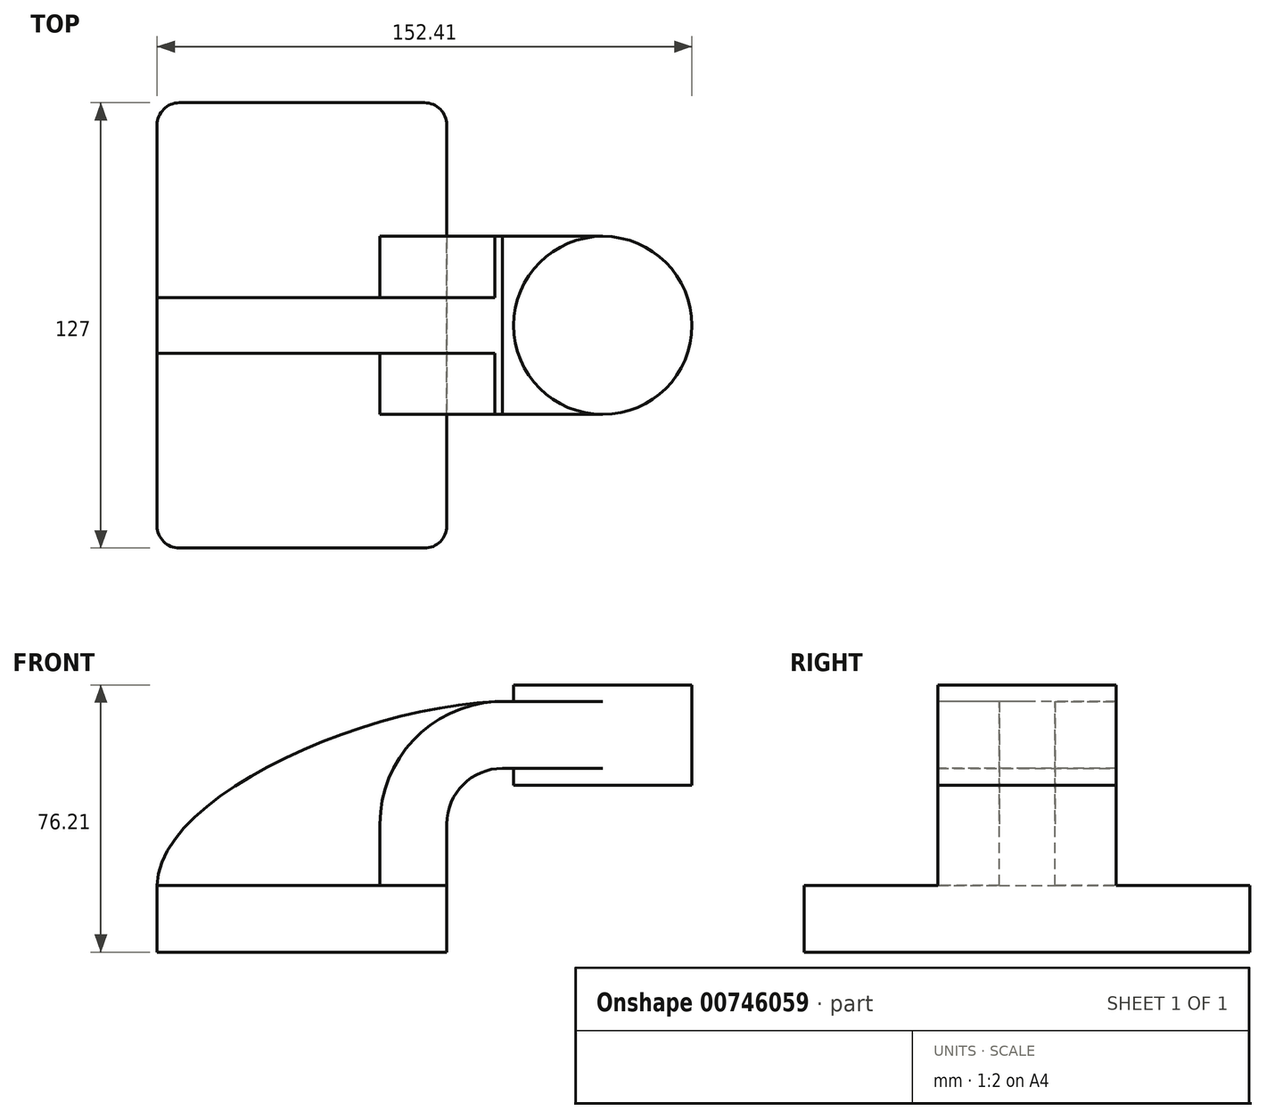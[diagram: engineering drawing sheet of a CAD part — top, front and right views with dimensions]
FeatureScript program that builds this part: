
annotation { "Feature Type Name" : "Feature", "Feature Type Description" : "" }
export const myFeature = defineFeature(function(context is Context, id is Id, definition is map)
    precondition{}
    {
        {
            var Q0;
            Q0=qCreatedBy(makeId("Front.planeOp"),FACE);
            var sketch = newSketch(context, id + "F0", { "sketchPlane" : qUnion([Q0])});
            skLineSegment(sketch, "E0.bottom", {"start": v(-41.28, -9.53) * mm, "end": v(41.28, -9.53) * mm});
            skLineSegment(sketch, "E0.top", {"start": v(-41.28, 9.53) * mm, "end": v(41.28, 9.53) * mm});
            skLineSegment(sketch, "E0.left", {"start": v(-41.28, -9.53) * mm, "end": v(-41.28, 9.53) * mm});
            skLineSegment(sketch, "E0.right", {"start": v(41.28, -9.53) * mm, "end": v(41.28, 9.53) * mm});
            skPoint(sketch, "E0.middle", {"position": v(0, 0) * mm});
            skLineSegment(sketch, "E1.bottom", {"start": v(60.32, 66.67) * mm, "end": v(111.12, 66.67) * mm});
            skLineSegment(sketch, "E1.top", {"start": v(60.32, 38.1) * mm, "end": v(111.12, 38.1) * mm});
            skLineSegment(sketch, "E1.left", {"start": v(60.32, 66.68) * mm, "end": v(60.32, 38.1) * mm});
            skLineSegment(sketch, "E1.right", {"start": v(111.12, 66.67) * mm, "end": v(111.12, 38.1) * mm});
            skPoint(sketch, "E1.middle", {"position": v(85.72, 52.39) * mm});
            skLineSegment(sketch, "E2", {"start": v(41.27, 9.53) * mm, "end": v(41.27, 27) * mm});
            skArc(sketch, "E3", {"start": v(41.27, 27) * mm, "mid": v(45.92, 38.23) * mm, "end": v(57.15, 42.88) * mm});
            skLineSegment(sketch, "E4", {"start": v(57.15, 42.88) * mm, "end": v(85.72, 42.88) * mm});
            skLineSegment(sketch, "E5.0", {"start": v(57.15, 61.93) * mm, "end": v(85.72, 61.93) * mm});
            skArc(sketch, "E5.1", {"start": v(22.22, 27) * mm, "mid": v(32.45, 51.7) * mm, "end": v(57.15, 61.93) * mm});
            skLineSegment(sketch, "E5.2", {"start": v(22.22, 9.53) * mm, "end": v(22.22, 27) * mm});
            skLineSegment(sketch, "E6", {"start": v(85.72, 38.1) * mm, "end": v(85.72, 66.67) * mm});
            skFitSpline(sketch, "E7", {"points": [v(-41.28, 9.53) * mm, v(57.15, 61.93) * mm], "startDerivative": vector(1.57, 77.31) * mm, "endDerivative": vector(114.86, 2.17) * mm});
            skSolve(sketch);
        }
        {
            var Q0;
            Q0=makeQuery(id+"F0.imprint","IMPRINT",FACE,{"disambiguationData":[TD([[makeQuery(id+"F0.imprint","IMPRINT",EDGE,{"derivedFrom":sQuery(id+"F0.wireOp",EDGE,"E0.bottom")}),1.0]])]});
            extrude(context, id + "F1", {"entities" : qUnion([Q0]), "endBound" : BoundingType.SYMMETRIC, "oppositeDirection" : true, "depth" : 127 * mm, "offsetDistance" : 25.4 * mm});
        }
        {
            var Q0;
            {var subQ1=sQuery(id+"F0.wireOp",EDGE,"E2");Q0=makeQuery(id+"F0.imprint","IMPRINT",FACE,{"disambiguationData":[TD([[makeQuery(id+"F0.imprint","IMPRINT",EDGE,{"derivedFrom":subQ1}),1.0]])]});}
            var Q1;
            {var subQ0=sQuery(id+"F0.wireOp",EDGE,"E5.0");var subQ1=sQuery(id+"F0.wireOp",EDGE,"E1.left");var subQ2=makeQuery(id+"F0.imprint","INTERSECT",VERTEX,{"derivedFrom":[subQ1,subQ0]});Q1=makeQuery(id+"F0.imprint","IMPRINT",FACE,{"disambiguationData":[TD([[makeQuery(id+"F0.imprint","IMPRINT",EDGE,{"disambiguationData":[TD([[subQ2,-1.0]])],"derivedFrom":subQ1}),1.0]])]});}
            extrude(context, id + "F2", {"entities" : qUnion([Q0, Q1]), "operationType" : NewBodyOperationType.ADD, "endBound" : BoundingType.SYMMETRIC, "depth" : 50.8 * mm, "offsetDistance" : 25.4 * mm});
        }
        {
            var Q0;
            {var subQ3=sQuery(id+"F0.wireOp",EDGE,"E5.2");Q0=makeQuery(id+"F0.imprint","IMPRINT",FACE,{"disambiguationData":[TD([[makeQuery(id+"F0.imprint","IMPRINT",EDGE,{"derivedFrom":subQ3}),1.0]])]});}
            extrude(context, id + "F3", {"entities" : qUnion([Q0]), "operationType" : NewBodyOperationType.ADD, "endBound" : BoundingType.SYMMETRIC, "depth" : 15.88 * mm, "offsetDistance" : 25.4 * mm});
        }
        {
            var Q0;
            {var subQ4=sQuery(id+"F0.wireOp",EDGE,"E1.right");Q0=makeQuery(id+"F0.imprint","IMPRINT",FACE,{"disambiguationData":[TD([[makeQuery(id+"F0.imprint","IMPRINT",EDGE,{"derivedFrom":subQ4}),-1.0]])]});}
            var Q1;
            Q1=sQuery(id+"F0.wireOp",EDGE,"E6");
            revolve(context, id + "F4", {"operationType" : NewBodyOperationType.ADD, "surfaceOperationType" : NewSurfaceOperationType.NEW, "entities" : qUnion([Q0]), "axis" : qUnion([Q1]), "revolveType" : RevolveType.FULL});
        }
        {
            var Q0;
            Q0=makeQuery(id+"F1.opExtrude","CAP_EDGE",EDGE,{"disambiguationData":[OSD([sQuery(id+"F0.wireOp",EDGE,"E0.left")])],"isStart":true});
            var Q1;
            Q1=makeQuery(id+"F1.opExtrude","CAP_EDGE",EDGE,{"disambiguationData":[OSD([sQuery(id+"F0.wireOp",EDGE,"E0.right")])],"isStart":true});
            var Q2;
            Q2=makeQuery(id+"F1.opExtrude","CAP_EDGE",EDGE,{"disambiguationData":[OSD([sQuery(id+"F0.wireOp",EDGE,"E0.right")])],"isStart":false});
            var Q3;
            Q3=makeQuery(id+"F1.opExtrude","CAP_EDGE",EDGE,{"disambiguationData":[OSD([sQuery(id+"F0.wireOp",EDGE,"E0.left")])],"isStart":false});
            fillet(context, id + "F5", {"entities" : qUnion([Q0, Q1, Q2, Q3]), "radius" : 6.35 * mm, "tangentPropagation" : true, "allowEdgeOverflow" : false});
        }
    });
